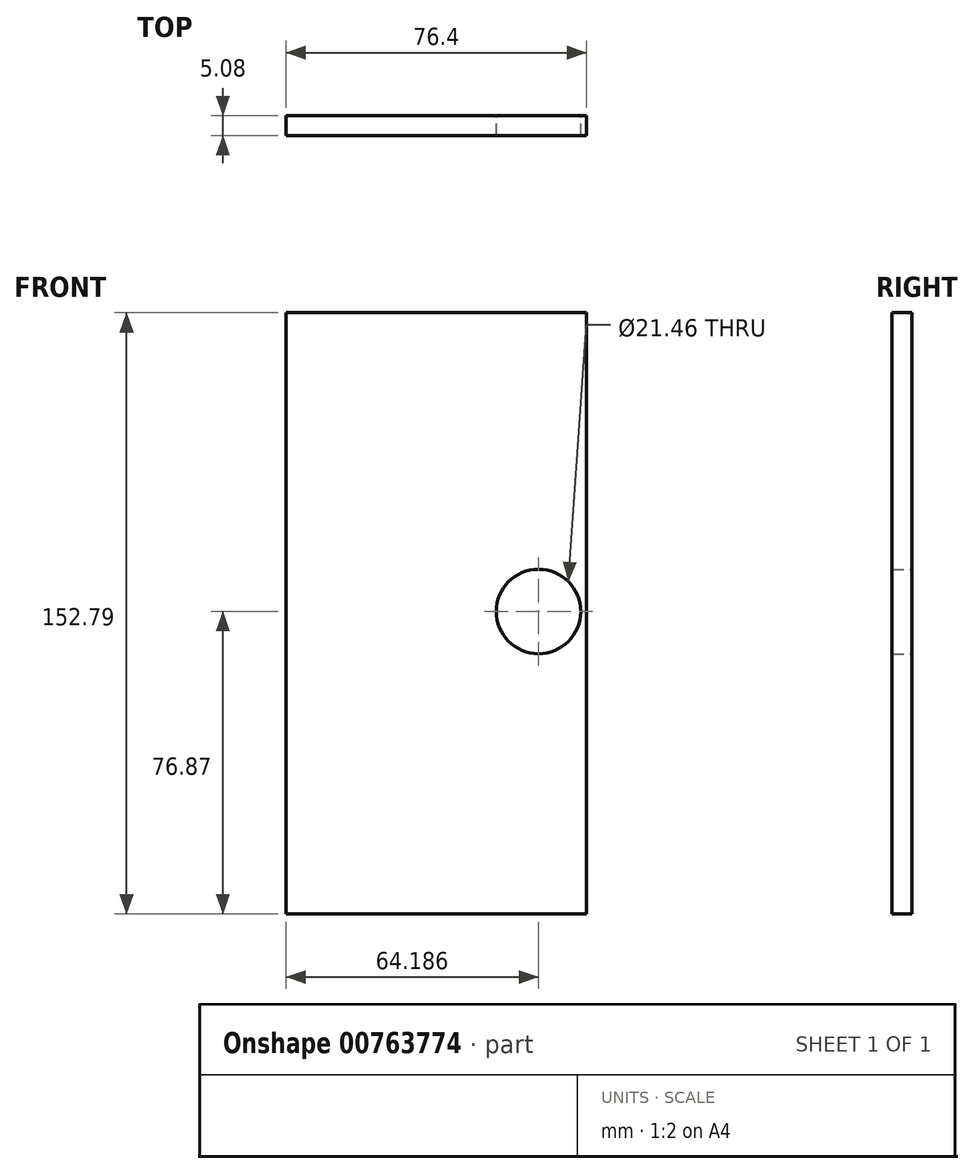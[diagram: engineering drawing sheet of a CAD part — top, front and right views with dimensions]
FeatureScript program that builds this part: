
annotation { "Feature Type Name" : "Feature", "Feature Type Description" : "" }
export const myFeature = defineFeature(function(context is Context, id is Id, definition is map)
    precondition{}
    {
        {
            var Q0;
            Q0=qCreatedBy(makeId("Front.planeOp"),FACE);
            var sketch = newSketch(context, id + "F0", { "sketchPlane" : qUnion([Q0])});
            skLineSegment(sketch, "E0.bottom", {"start": v(-76.4, 75.92) * mm, "end": v(0, 75.92) * mm});
            skLineSegment(sketch, "E0.top", {"start": v(-76.4, -76.87) * mm, "end": v(0, -76.87) * mm});
            skLineSegment(sketch, "E0.left", {"start": v(-76.4, 75.92) * mm, "end": v(-76.4, -76.87) * mm});
            skLineSegment(sketch, "E0.right", {"start": v(0, 75.92) * mm, "end": v(0, -76.87) * mm});
            skCircle(sketch, "E1", {"center": v(-12.21, 0) * mm, "radius": 10.73 * mm});
            skSolve(sketch);
        }
        {
            var Q0;
            Q0=makeQuery(id+"F0.imprint","IMPRINT",FACE,{"disambiguationData":[TD([[makeQuery(id+"F0.imprint","IMPRINT",EDGE,{"derivedFrom":sQuery(id+"F0.wireOp",EDGE,"E0.bottom")}),-1.0]])]});
            extrude(context, id + "F1", {"entities" : qUnion([Q0]), "depth" : 5.08 * mm, "offsetDistance" : 25.4 * mm});
        }
    });
